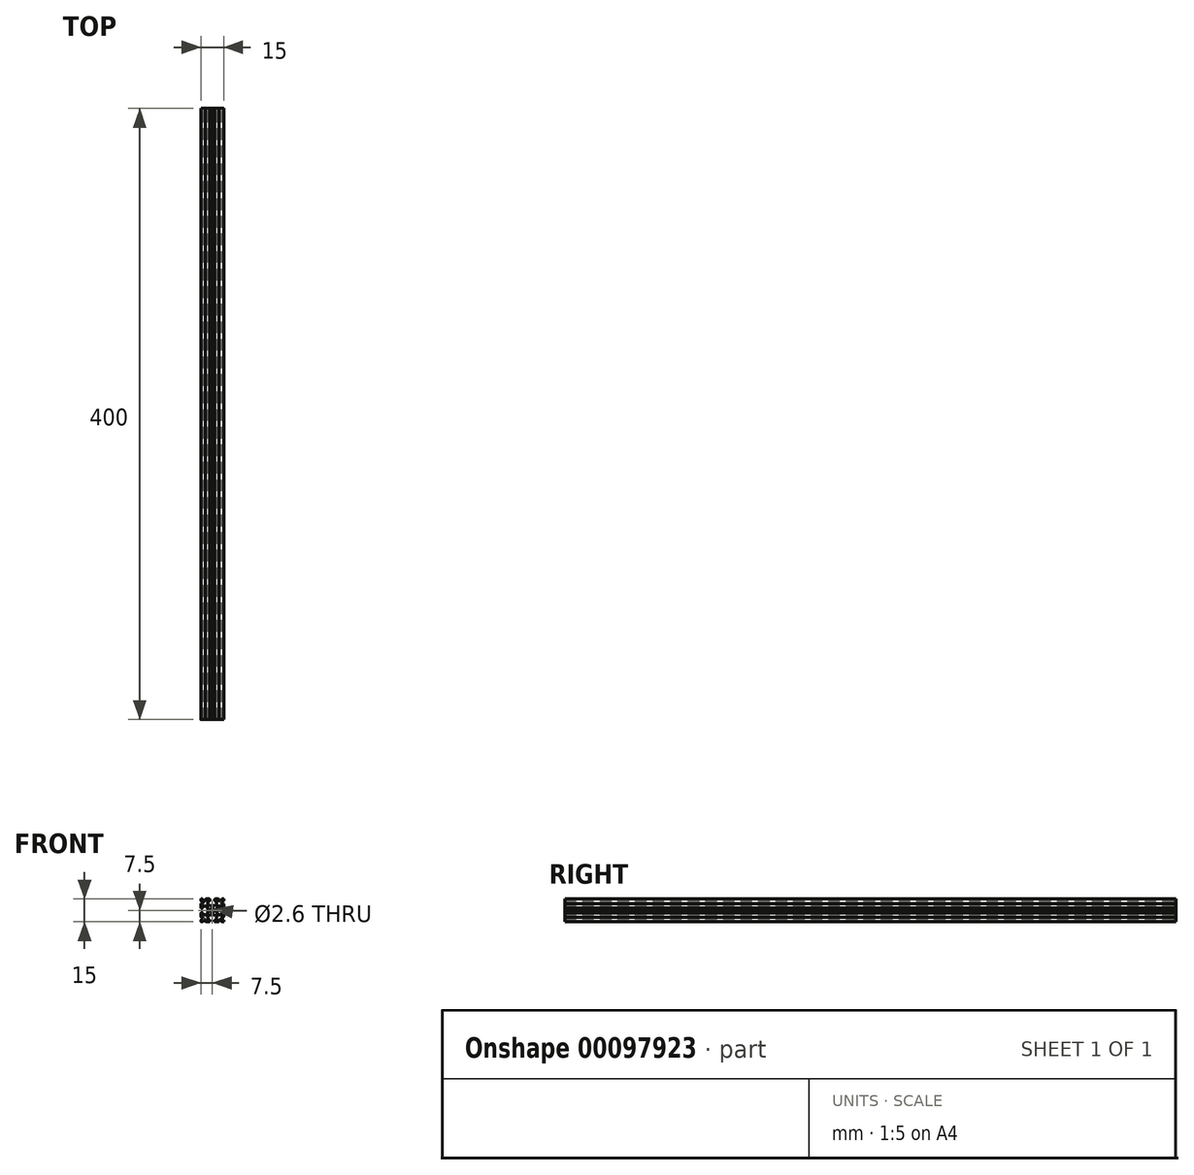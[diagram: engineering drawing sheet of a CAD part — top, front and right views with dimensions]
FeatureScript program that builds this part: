
annotation { "Feature Type Name" : "Feature", "Feature Type Description" : "" }
export const myFeature = defineFeature(function(context is Context, id is Id, definition is map)
    precondition{}
    {
        {
            var Q0;
            Q0=qCreatedBy(makeId("Front.planeOp"),FACE);
            var sketch = newSketch(context, id + "F0", { "sketchPlane" : qUnion([Q0])});
            skLineSegment(sketch, "E0.0.0", {"start": v(0.83, -2.55) * mm, "end": v(0.83, -2.77) * mm});
            skArc(sketch, "E0.0.1", {"start": v(0.83, -2.77) * mm, "mid": v(0.87, -2.9) * mm, "end": v(0.98, -2.97) * mm});
            skLineSegment(sketch, "E0.0.2", {"start": v(0.98, -2.97) * mm, "end": v(2.5, -3.31) * mm});
            skArc(sketch, "E0.0.3", {"start": v(2.5, -3.31) * mm, "mid": v(2.8, -3.49) * mm, "end": v(2.9, -3.8) * mm});
            skLineSegment(sketch, "E0.0.4", {"start": v(2.9, -3.8) * mm, "end": v(2.9, -5.9) * mm});
            skArc(sketch, "E0.0.5", {"start": v(2.9, -5.9) * mm, "mid": v(2.84, -6.04) * mm, "end": v(2.7, -6.1) * mm});
            skLineSegment(sketch, "E0.0.6", {"start": v(2.7, -6.1) * mm, "end": v(2.1, -6.1) * mm});
            skArc(sketch, "E0.0.7", {"start": v(2.1, -6.1) * mm, "mid": v(1.75, -6.25) * mm, "end": v(1.6, -6.6) * mm});
            skLineSegment(sketch, "E0.0.8", {"start": v(1.6, -6.6) * mm, "end": v(1.6, -7) * mm});
            skArc(sketch, "E0.0.9", {"start": v(1.6, -7) * mm, "mid": v(1.75, -7.35) * mm, "end": v(2.1, -7.5) * mm});
            skLineSegment(sketch, "E0.0.10", {"start": v(2.1, -7.5) * mm, "end": v(3.9, -7.5) * mm});
            skArc(sketch, "E0.0.11", {"start": v(3.9, -7.5) * mm, "mid": v(4.25, -7.35) * mm, "end": v(4.4, -7) * mm});
            skLineSegment(sketch, "E0.0.12", {"start": v(4.4, -7) * mm, "end": v(4.4, -6.67) * mm});
            skArc(sketch, "E0.0.13", {"start": v(4.4, -6.67) * mm, "mid": v(4.7, -6.2) * mm, "end": v(5.25, -6.31) * mm});
            skLineSegment(sketch, "E0.0.14", {"start": v(5.25, -6.31) * mm, "end": v(6.3, -7.35) * mm});
            skArc(sketch, "E0.0.15", {"start": v(6.3, -7.35) * mm, "mid": v(6.46, -7.46) * mm, "end": v(6.65, -7.5) * mm});
            skLineSegment(sketch, "E0.0.16", {"start": v(6.65, -7.5) * mm, "end": v(7.25, -7.5) * mm});
            skArc(sketch, "E0.0.17", {"start": v(7.25, -7.5) * mm, "mid": v(7.43, -7.43) * mm, "end": v(7.5, -7.25) * mm});
            skLineSegment(sketch, "E0.0.18", {"start": v(7.5, -7.25) * mm, "end": v(7.5, -6.65) * mm});
            skArc(sketch, "E0.0.19", {"start": v(7.5, -6.65) * mm, "mid": v(7.46, -6.46) * mm, "end": v(7.35, -6.3) * mm});
            skLineSegment(sketch, "E0.0.20", {"start": v(7.35, -6.3) * mm, "end": v(6.31, -5.25) * mm});
            skArc(sketch, "E0.0.21", {"start": v(6.31, -5.25) * mm, "mid": v(6.2, -4.7) * mm, "end": v(6.67, -4.4) * mm});
            skLineSegment(sketch, "E0.0.22", {"start": v(6.67, -4.4) * mm, "end": v(7, -4.4) * mm});
            skArc(sketch, "E0.0.23", {"start": v(7, -4.4) * mm, "mid": v(7.35, -4.25) * mm, "end": v(7.5, -3.9) * mm});
            skLineSegment(sketch, "E0.0.24", {"start": v(7.5, -3.9) * mm, "end": v(7.5, -2.1) * mm});
            skArc(sketch, "E0.0.25", {"start": v(7.5, -2.1) * mm, "mid": v(7.35, -1.75) * mm, "end": v(7, -1.6) * mm});
            skLineSegment(sketch, "E0.0.26", {"start": v(7, -1.6) * mm, "end": v(6.6, -1.6) * mm});
            skArc(sketch, "E0.0.27", {"start": v(6.6, -1.6) * mm, "mid": v(6.25, -1.75) * mm, "end": v(6.1, -2.1) * mm});
            skLineSegment(sketch, "E0.0.28", {"start": v(6.1, -2.1) * mm, "end": v(6.1, -2.7) * mm});
            skArc(sketch, "E0.0.29", {"start": v(6.1, -2.7) * mm, "mid": v(6.04, -2.84) * mm, "end": v(5.9, -2.9) * mm});
            skLineSegment(sketch, "E0.0.30", {"start": v(5.9, -2.9) * mm, "end": v(3.8, -2.9) * mm});
            skArc(sketch, "E0.0.31", {"start": v(3.8, -2.9) * mm, "mid": v(3.49, -2.8) * mm, "end": v(3.31, -2.5) * mm});
            skLineSegment(sketch, "E0.0.32", {"start": v(3.31, -2.5) * mm, "end": v(2.97, -0.98) * mm});
            skArc(sketch, "E0.0.33", {"start": v(2.97, -0.98) * mm, "mid": v(2.9, -0.87) * mm, "end": v(2.77, -0.83) * mm});
            skLineSegment(sketch, "E0.0.34", {"start": v(2.77, -0.83) * mm, "end": v(2.55, -0.83) * mm});
            skArc(sketch, "E0.0.35", {"start": v(2.55, -0.83) * mm, "mid": v(2.4, -0.77) * mm, "end": v(2.35, -0.63) * mm});
            skLineSegment(sketch, "E0.0.36", {"start": v(2.35, -0.63) * mm, "end": v(2.35, 0.63) * mm});
            skArc(sketch, "E0.0.37", {"start": v(2.35, 0.63) * mm, "mid": v(2.4, 0.77) * mm, "end": v(2.55, 0.83) * mm});
            skLineSegment(sketch, "E0.0.38", {"start": v(2.55, 0.83) * mm, "end": v(2.77, 0.83) * mm});
            skArc(sketch, "E0.0.39", {"start": v(2.77, 0.83) * mm, "mid": v(2.9, 0.87) * mm, "end": v(2.97, 0.98) * mm});
            skLineSegment(sketch, "E0.0.40", {"start": v(2.97, 0.98) * mm, "end": v(3.31, 2.5) * mm});
            skArc(sketch, "E0.0.41", {"start": v(3.31, 2.5) * mm, "mid": v(3.49, 2.8) * mm, "end": v(3.8, 2.9) * mm});
            skLineSegment(sketch, "E0.0.42", {"start": v(3.8, 2.9) * mm, "end": v(5.9, 2.9) * mm});
            skArc(sketch, "E0.0.43", {"start": v(5.9, 2.9) * mm, "mid": v(6.04, 2.84) * mm, "end": v(6.1, 2.7) * mm});
            skLineSegment(sketch, "E0.0.44", {"start": v(6.1, 2.7) * mm, "end": v(6.1, 2.1) * mm});
            skArc(sketch, "E0.0.45", {"start": v(6.1, 2.1) * mm, "mid": v(6.25, 1.75) * mm, "end": v(6.6, 1.6) * mm});
            skLineSegment(sketch, "E0.0.46", {"start": v(6.6, 1.6) * mm, "end": v(7, 1.6) * mm});
            skArc(sketch, "E0.0.47", {"start": v(7, 1.6) * mm, "mid": v(7.35, 1.75) * mm, "end": v(7.5, 2.1) * mm});
            skLineSegment(sketch, "E0.0.48", {"start": v(7.5, 2.1) * mm, "end": v(7.5, 3.9) * mm});
            skArc(sketch, "E0.0.49", {"start": v(7.5, 3.9) * mm, "mid": v(7.35, 4.25) * mm, "end": v(7, 4.4) * mm});
            skLineSegment(sketch, "E0.0.50", {"start": v(7, 4.4) * mm, "end": v(6.67, 4.4) * mm});
            skArc(sketch, "E0.0.51", {"start": v(6.67, 4.4) * mm, "mid": v(6.2, 4.7) * mm, "end": v(6.31, 5.25) * mm});
            skLineSegment(sketch, "E0.0.52", {"start": v(6.31, 5.25) * mm, "end": v(7.35, 6.3) * mm});
            skArc(sketch, "E0.0.53", {"start": v(7.35, 6.3) * mm, "mid": v(7.46, 6.46) * mm, "end": v(7.5, 6.65) * mm});
            skLineSegment(sketch, "E0.0.54", {"start": v(7.5, 6.65) * mm, "end": v(7.5, 7.25) * mm});
            skArc(sketch, "E0.0.55", {"start": v(7.5, 7.25) * mm, "mid": v(7.43, 7.43) * mm, "end": v(7.25, 7.5) * mm});
            skLineSegment(sketch, "E0.0.56", {"start": v(7.25, 7.5) * mm, "end": v(6.65, 7.5) * mm});
            skArc(sketch, "E0.0.57", {"start": v(6.65, 7.5) * mm, "mid": v(6.46, 7.46) * mm, "end": v(6.3, 7.35) * mm});
            skLineSegment(sketch, "E0.0.58", {"start": v(6.3, 7.35) * mm, "end": v(5.25, 6.31) * mm});
            skArc(sketch, "E0.0.59", {"start": v(5.25, 6.31) * mm, "mid": v(4.7, 6.2) * mm, "end": v(4.4, 6.67) * mm});
            skLineSegment(sketch, "E0.0.60", {"start": v(4.4, 6.67) * mm, "end": v(4.4, 7) * mm});
            skArc(sketch, "E0.0.61", {"start": v(4.4, 7) * mm, "mid": v(4.25, 7.35) * mm, "end": v(3.9, 7.5) * mm});
            skLineSegment(sketch, "E0.0.62", {"start": v(3.9, 7.5) * mm, "end": v(2.1, 7.5) * mm});
            skArc(sketch, "E0.0.63", {"start": v(2.1, 7.5) * mm, "mid": v(1.75, 7.35) * mm, "end": v(1.6, 7) * mm});
            skLineSegment(sketch, "E0.0.64", {"start": v(1.6, 7) * mm, "end": v(1.6, 6.6) * mm});
            skArc(sketch, "E0.0.65", {"start": v(1.6, 6.6) * mm, "mid": v(1.75, 6.25) * mm, "end": v(2.1, 6.1) * mm});
            skLineSegment(sketch, "E0.0.66", {"start": v(2.1, 6.1) * mm, "end": v(2.7, 6.1) * mm});
            skArc(sketch, "E0.0.67", {"start": v(2.7, 6.1) * mm, "mid": v(2.84, 6.04) * mm, "end": v(2.9, 5.9) * mm});
            skLineSegment(sketch, "E0.0.68", {"start": v(2.9, 5.9) * mm, "end": v(2.9, 3.8) * mm});
            skArc(sketch, "E0.0.69", {"start": v(2.9, 3.8) * mm, "mid": v(2.8, 3.49) * mm, "end": v(2.5, 3.31) * mm});
            skLineSegment(sketch, "E0.0.70", {"start": v(2.5, 3.31) * mm, "end": v(0.98, 2.97) * mm});
            skArc(sketch, "E0.0.71", {"start": v(0.98, 2.97) * mm, "mid": v(0.87, 2.9) * mm, "end": v(0.83, 2.77) * mm});
            skLineSegment(sketch, "E0.0.72", {"start": v(0.83, 2.77) * mm, "end": v(0.83, 2.55) * mm});
            skArc(sketch, "E0.0.73", {"start": v(0.83, 2.55) * mm, "mid": v(0.77, 2.4) * mm, "end": v(0.63, 2.35) * mm});
            skLineSegment(sketch, "E0.0.74", {"start": v(0.63, 2.35) * mm, "end": v(-0.63, 2.35) * mm});
            skArc(sketch, "E0.0.75", {"start": v(-0.63, 2.35) * mm, "mid": v(-0.77, 2.4) * mm, "end": v(-0.83, 2.55) * mm});
            skLineSegment(sketch, "E0.0.76", {"start": v(-0.83, 2.55) * mm, "end": v(-0.83, 2.77) * mm});
            skArc(sketch, "E0.0.77", {"start": v(-0.83, 2.77) * mm, "mid": v(-0.87, 2.9) * mm, "end": v(-0.98, 2.97) * mm});
            skLineSegment(sketch, "E0.0.78", {"start": v(-0.98, 2.97) * mm, "end": v(-2.5, 3.31) * mm});
            skArc(sketch, "E0.0.79", {"start": v(-2.5, 3.31) * mm, "mid": v(-2.8, 3.49) * mm, "end": v(-2.9, 3.8) * mm});
            skLineSegment(sketch, "E0.0.80", {"start": v(-2.9, 3.8) * mm, "end": v(-2.9, 5.9) * mm});
            skArc(sketch, "E0.0.81", {"start": v(-2.9, 5.9) * mm, "mid": v(-2.84, 6.04) * mm, "end": v(-2.7, 6.1) * mm});
            skLineSegment(sketch, "E0.0.82", {"start": v(-2.7, 6.1) * mm, "end": v(-2.1, 6.1) * mm});
            skArc(sketch, "E0.0.83", {"start": v(-2.1, 6.1) * mm, "mid": v(-1.75, 6.25) * mm, "end": v(-1.6, 6.6) * mm});
            skLineSegment(sketch, "E0.0.84", {"start": v(-1.6, 6.6) * mm, "end": v(-1.6, 7) * mm});
            skArc(sketch, "E0.0.85", {"start": v(-1.6, 7) * mm, "mid": v(-1.75, 7.35) * mm, "end": v(-2.1, 7.5) * mm});
            skLineSegment(sketch, "E0.0.86", {"start": v(-2.1, 7.5) * mm, "end": v(-3.9, 7.5) * mm});
            skArc(sketch, "E0.0.87", {"start": v(-3.9, 7.5) * mm, "mid": v(-4.25, 7.35) * mm, "end": v(-4.4, 7) * mm});
            skLineSegment(sketch, "E0.0.88", {"start": v(-4.4, 7) * mm, "end": v(-4.4, 6.67) * mm});
            skArc(sketch, "E0.0.89", {"start": v(-4.4, 6.67) * mm, "mid": v(-4.7, 6.2) * mm, "end": v(-5.25, 6.31) * mm});
            skLineSegment(sketch, "E0.0.90", {"start": v(-5.25, 6.31) * mm, "end": v(-6.3, 7.35) * mm});
            skArc(sketch, "E0.0.91", {"start": v(-6.3, 7.35) * mm, "mid": v(-6.46, 7.46) * mm, "end": v(-6.65, 7.5) * mm});
            skLineSegment(sketch, "E0.0.92", {"start": v(-6.65, 7.5) * mm, "end": v(-7.25, 7.5) * mm});
            skArc(sketch, "E0.0.93", {"start": v(-7.25, 7.5) * mm, "mid": v(-7.43, 7.43) * mm, "end": v(-7.5, 7.25) * mm});
            skLineSegment(sketch, "E0.0.94", {"start": v(-7.5, 7.25) * mm, "end": v(-7.5, 6.65) * mm});
            skArc(sketch, "E0.0.95", {"start": v(-7.5, 6.65) * mm, "mid": v(-7.46, 6.46) * mm, "end": v(-7.35, 6.3) * mm});
            skLineSegment(sketch, "E0.0.96", {"start": v(-7.35, 6.3) * mm, "end": v(-6.31, 5.25) * mm});
            skArc(sketch, "E0.0.97", {"start": v(-6.31, 5.25) * mm, "mid": v(-6.2, 4.7) * mm, "end": v(-6.67, 4.4) * mm});
            skLineSegment(sketch, "E0.0.98", {"start": v(-6.67, 4.4) * mm, "end": v(-7, 4.4) * mm});
            skArc(sketch, "E0.0.99", {"start": v(-7, 4.4) * mm, "mid": v(-7.35, 4.25) * mm, "end": v(-7.5, 3.9) * mm});
            skLineSegment(sketch, "E0.0.100", {"start": v(-7.5, 3.9) * mm, "end": v(-7.5, 2.1) * mm});
            skArc(sketch, "E0.0.101", {"start": v(-7.5, 2.1) * mm, "mid": v(-7.35, 1.75) * mm, "end": v(-7, 1.6) * mm});
            skLineSegment(sketch, "E0.0.102", {"start": v(-7, 1.6) * mm, "end": v(-6.6, 1.6) * mm});
            skArc(sketch, "E0.0.103", {"start": v(-6.6, 1.6) * mm, "mid": v(-6.25, 1.75) * mm, "end": v(-6.1, 2.1) * mm});
            skLineSegment(sketch, "E0.0.104", {"start": v(-6.1, 2.1) * mm, "end": v(-6.1, 2.7) * mm});
            skArc(sketch, "E0.0.105", {"start": v(-6.1, 2.7) * mm, "mid": v(-6.04, 2.84) * mm, "end": v(-5.9, 2.9) * mm});
            skLineSegment(sketch, "E0.0.106", {"start": v(-5.9, 2.9) * mm, "end": v(-3.8, 2.9) * mm});
            skArc(sketch, "E0.0.107", {"start": v(-3.8, 2.9) * mm, "mid": v(-3.49, 2.8) * mm, "end": v(-3.31, 2.5) * mm});
            skLineSegment(sketch, "E0.0.108", {"start": v(-3.31, 2.5) * mm, "end": v(-2.97, 0.98) * mm});
            skArc(sketch, "E0.0.109", {"start": v(-2.97, 0.98) * mm, "mid": v(-2.9, 0.87) * mm, "end": v(-2.77, 0.83) * mm});
            skLineSegment(sketch, "E0.0.110", {"start": v(-2.77, 0.83) * mm, "end": v(-2.55, 0.83) * mm});
            skArc(sketch, "E0.0.111", {"start": v(-2.55, 0.83) * mm, "mid": v(-2.4, 0.77) * mm, "end": v(-2.35, 0.63) * mm});
            skLineSegment(sketch, "E0.0.112", {"start": v(-2.35, 0.63) * mm, "end": v(-2.35, -0.63) * mm});
            skArc(sketch, "E0.0.113", {"start": v(-2.35, -0.63) * mm, "mid": v(-2.4, -0.77) * mm, "end": v(-2.55, -0.83) * mm});
            skLineSegment(sketch, "E0.0.114", {"start": v(-2.55, -0.83) * mm, "end": v(-2.77, -0.83) * mm});
            skArc(sketch, "E0.0.115", {"start": v(-2.77, -0.83) * mm, "mid": v(-2.9, -0.87) * mm, "end": v(-2.97, -0.98) * mm});
            skLineSegment(sketch, "E0.0.116", {"start": v(-2.97, -0.98) * mm, "end": v(-3.31, -2.5) * mm});
            skArc(sketch, "E0.0.117", {"start": v(-3.31, -2.5) * mm, "mid": v(-3.49, -2.8) * mm, "end": v(-3.8, -2.9) * mm});
            skLineSegment(sketch, "E0.0.118", {"start": v(-3.8, -2.9) * mm, "end": v(-5.9, -2.9) * mm});
            skArc(sketch, "E0.0.119", {"start": v(-5.9, -2.9) * mm, "mid": v(-6.04, -2.84) * mm, "end": v(-6.1, -2.7) * mm});
            skLineSegment(sketch, "E0.0.120", {"start": v(-6.1, -2.7) * mm, "end": v(-6.1, -2.1) * mm});
            skArc(sketch, "E0.0.121", {"start": v(-6.1, -2.1) * mm, "mid": v(-6.25, -1.75) * mm, "end": v(-6.6, -1.6) * mm});
            skLineSegment(sketch, "E0.0.122", {"start": v(-6.6, -1.6) * mm, "end": v(-7, -1.6) * mm});
            skArc(sketch, "E0.0.123", {"start": v(-7, -1.6) * mm, "mid": v(-7.35, -1.75) * mm, "end": v(-7.5, -2.1) * mm});
            skLineSegment(sketch, "E0.0.124", {"start": v(-7.5, -2.1) * mm, "end": v(-7.5, -3.9) * mm});
            skArc(sketch, "E0.0.125", {"start": v(-7.5, -3.9) * mm, "mid": v(-7.35, -4.25) * mm, "end": v(-7, -4.4) * mm});
            skLineSegment(sketch, "E0.0.126", {"start": v(-7, -4.4) * mm, "end": v(-6.67, -4.4) * mm});
            skArc(sketch, "E0.0.127", {"start": v(-6.67, -4.4) * mm, "mid": v(-6.2, -4.7) * mm, "end": v(-6.31, -5.25) * mm});
            skLineSegment(sketch, "E0.0.128", {"start": v(-6.31, -5.25) * mm, "end": v(-7.35, -6.3) * mm});
            skArc(sketch, "E0.0.129", {"start": v(-7.35, -6.3) * mm, "mid": v(-7.46, -6.46) * mm, "end": v(-7.5, -6.65) * mm});
            skLineSegment(sketch, "E0.0.130", {"start": v(-7.5, -6.65) * mm, "end": v(-7.5, -7.25) * mm});
            skArc(sketch, "E0.0.131", {"start": v(-7.5, -7.25) * mm, "mid": v(-7.43, -7.43) * mm, "end": v(-7.25, -7.5) * mm});
            skLineSegment(sketch, "E0.0.132", {"start": v(-7.25, -7.5) * mm, "end": v(-6.65, -7.5) * mm});
            skArc(sketch, "E0.0.133", {"start": v(-6.65, -7.5) * mm, "mid": v(-6.46, -7.46) * mm, "end": v(-6.3, -7.35) * mm});
            skLineSegment(sketch, "E0.0.134", {"start": v(-6.3, -7.35) * mm, "end": v(-5.25, -6.31) * mm});
            skArc(sketch, "E0.0.135", {"start": v(-5.25, -6.31) * mm, "mid": v(-4.7, -6.2) * mm, "end": v(-4.4, -6.67) * mm});
            skLineSegment(sketch, "E0.0.136", {"start": v(-4.4, -6.67) * mm, "end": v(-4.4, -7) * mm});
            skArc(sketch, "E0.0.137", {"start": v(-4.4, -7) * mm, "mid": v(-4.25, -7.35) * mm, "end": v(-3.9, -7.5) * mm});
            skLineSegment(sketch, "E0.0.138", {"start": v(-3.9, -7.5) * mm, "end": v(-2.1, -7.5) * mm});
            skArc(sketch, "E0.0.139", {"start": v(-2.1, -7.5) * mm, "mid": v(-1.75, -7.35) * mm, "end": v(-1.6, -7) * mm});
            skLineSegment(sketch, "E0.0.140", {"start": v(-1.6, -7) * mm, "end": v(-1.6, -6.6) * mm});
            skArc(sketch, "E0.0.141", {"start": v(-1.6, -6.6) * mm, "mid": v(-1.75, -6.25) * mm, "end": v(-2.1, -6.1) * mm});
            skLineSegment(sketch, "E0.0.142", {"start": v(-2.1, -6.1) * mm, "end": v(-2.7, -6.1) * mm});
            skArc(sketch, "E0.0.143", {"start": v(-2.7, -6.1) * mm, "mid": v(-2.84, -6.04) * mm, "end": v(-2.9, -5.9) * mm});
            skLineSegment(sketch, "E0.0.144", {"start": v(-2.9, -5.9) * mm, "end": v(-2.9, -3.8) * mm});
            skArc(sketch, "E0.0.145", {"start": v(-2.9, -3.8) * mm, "mid": v(-2.8, -3.49) * mm, "end": v(-2.5, -3.31) * mm});
            skLineSegment(sketch, "E0.0.146", {"start": v(-2.5, -3.31) * mm, "end": v(-0.98, -2.97) * mm});
            skArc(sketch, "E0.0.147", {"start": v(-0.98, -2.97) * mm, "mid": v(-0.87, -2.9) * mm, "end": v(-0.83, -2.77) * mm});
            skLineSegment(sketch, "E0.0.148", {"start": v(-0.83, -2.77) * mm, "end": v(-0.83, -2.55) * mm});
            skArc(sketch, "E0.0.149", {"start": v(-0.83, -2.55) * mm, "mid": v(-0.77, -2.4) * mm, "end": v(-0.63, -2.35) * mm});
            skLineSegment(sketch, "E0.0.150", {"start": v(-0.63, -2.35) * mm, "end": v(0.63, -2.35) * mm});
            skArc(sketch, "E0.0.151", {"start": v(0.63, -2.35) * mm, "mid": v(0.77, -2.4) * mm, "end": v(0.83, -2.55) * mm});
            skPoint(sketch, "E1", {"position": v(0, 0) * mm});
            skPoint(sketch, "E1.positionSnap0", {"position": v(0, 2.35) * mm});
            skPoint(sketch, "E1.positionSnap1", {"position": v(2.35, 0) * mm});
            skCircle(sketch, "E2", {"center": v(0, 0) * mm, "radius": 1.3 * mm});
            skSolve(sketch);
        }
        {
            var Q0;
            Q0=makeQuery(id+"F0.imprint","IMPRINT",FACE,{"disambiguationData":[TD([[makeQuery(id+"F0.imprint","IMPRINT",EDGE,{"derivedFrom":sQuery(id+"F0.wireOp",EDGE,"E0.0.0")}),1.0]])]});
            extrude(context, id + "F1", {"entities" : qUnion([Q0]), "endBound" : BoundingType.SYMMETRIC, "depth" : 400 * mm});
        }
    });
